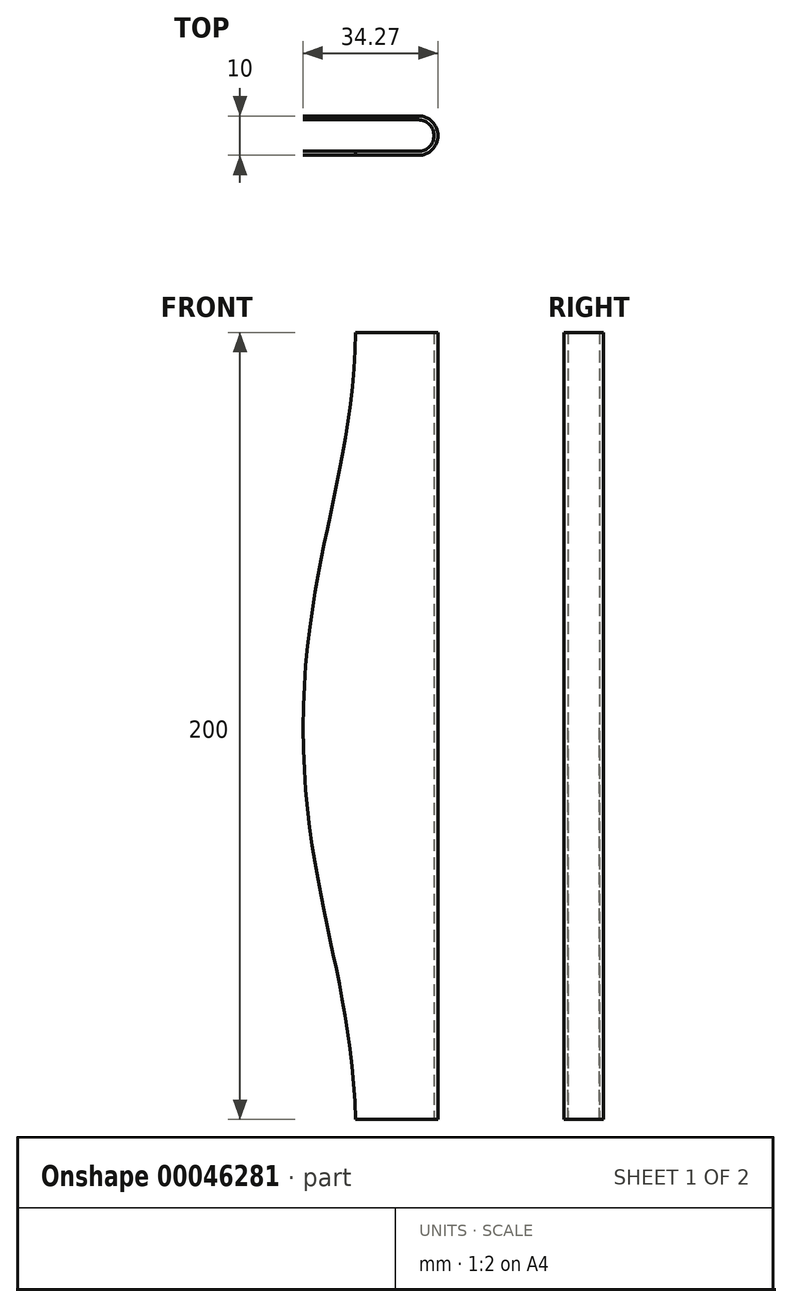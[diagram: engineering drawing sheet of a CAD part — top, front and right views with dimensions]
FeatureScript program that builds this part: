
annotation { "Feature Type Name" : "Feature", "Feature Type Description" : "" }
export const myFeature = defineFeature(function(context is Context, id is Id, definition is map)
    precondition{}
    {
        {
            var Q0;
            Q0=qCreatedBy(makeId("Top.planeOp"),FACE);
            var sketch = newSketch(context, id + "F0", { "sketchPlane" : qUnion([Q0])});
            skArc(sketch, "E0", {"start": v(0, -4) * mm, "mid": v(4, 0) * mm, "end": v(0, 4) * mm});
            skLineSegment(sketch, "E1", {"start": v(0, 0) * mm, "end": v(0, 4) * mm, "construction": true});
            skLineSegment(sketch, "E2", {"start": v(0, 4) * mm, "end": v(-30.1, 4) * mm});
            skLineSegment(sketch, "E3", {"start": v(0, 0) * mm, "end": v(-14, 0) * mm, "construction": true});
            skLineSegment(sketch, "E4", {"start": v(0, 0) * mm, "end": v(0, -4) * mm, "construction": true});
            skLineSegment(sketch, "E5.MirrorCS", {"start": v(0, -4) * mm, "end": v(-30.1, -4) * mm});
            skLineSegment(sketch, "E6.0", {"start": v(0, 5) * mm, "end": v(-30.1, 5) * mm});
            skArc(sketch, "E6.1", {"start": v(0, -5) * mm, "mid": v(5, 0) * mm, "end": v(0, 5) * mm});
            skLineSegment(sketch, "E6.2", {"start": v(0, -5) * mm, "end": v(-30.1, -5) * mm});
            skLineSegment(sketch, "E7", {"start": v(-30.1, 4) * mm, "end": v(-30.1, 5) * mm});
            skLineSegment(sketch, "E8", {"start": v(-30.1, -4) * mm, "end": v(-30.1, -5) * mm});
            skSolve(sketch);
        }
        {
            var Q0;
            Q0=makeQuery(id+"F0.imprint","IMPRINT",FACE,{"disambiguationData":[TD([[makeQuery(id+"F0.imprint","IMPRINT",EDGE,{"derivedFrom":sQuery(id+"F0.wireOp",EDGE,"E0")}),-1.0]])]});
            extrude(context, id + "F1", {"entities" : qUnion([Q0]), "depth" : 200 * mm});
        }
        {
            var Q0;
            Q0=qCreatedBy(makeId("Front.planeOp"),FACE);
            var sketch = newSketch(context, id + "F2", { "sketchPlane" : qUnion([Q0])});
            skLineSegment(sketch, "E9", {"start": v(0, 200.25) * mm, "end": v(-15.93, 200.25) * mm, "construction": true});
            skLineSegment(sketch, "E10", {"start": v(-15.93, 200.25) * mm, "end": v(-15.93, 211.97) * mm});
            skLineSegment(sketch, "E11", {"start": v(0, 200.25) * mm, "end": v(0, 99.54) * mm});
            skLineSegment(sketch, "E12", {"start": v(0, 99.54) * mm, "end": v(-39.41, 99.54) * mm, "construction": true});
            skLineSegment(sketch, "E13", {"start": v(-29.27, 99.54) * mm, "end": v(-29.27, 84.1) * mm, "construction": true});
            skFitSpline(sketch, "E14", {"points": [v(-15.93, 200.25) * mm, v(-19.73, 166.47) * mm, v(-25.1, 140.16) * mm, v(-29.27, 99.54) * mm], "startDerivative": vector(-1.09, -107.09) * mm, "endDerivative": vector(-0.1, -128.78) * mm});
            skFitSpline(sketch, "E15.MirrorCS", {"points": [v(-15.93, -1.17) * mm, v(-19.73, 32.61) * mm, v(-25.1, 58.91) * mm, v(-29.27, 99.54) * mm], "startDerivative": vector(-1.09, 107.09) * mm, "endDerivative": vector(-0.1, 128.78) * mm});
            skLineSegment(sketch, "E16.MirrorCS", {"start": v(-15.93, -1.17) * mm, "end": v(-15.93, -12.9) * mm});
            skLineSegment(sketch, "E17", {"start": v(-15.93, 211.97) * mm, "end": v(-58.8, 211.97) * mm});
            skLineSegment(sketch, "E18", {"start": v(-58.8, 211.97) * mm, "end": v(-58.8, -9.85) * mm});
            skLineSegment(sketch, "E19", {"start": v(-15.93, -12.9) * mm, "end": v(-58.8, -9.85) * mm});
            skSolve(sketch);
        }
        {
            var Q0;
            Q0=makeQuery(id+"F2.imprint","IMPRINT",FACE,{"disambiguationData":[TD([[makeQuery(id+"F2.imprint","IMPRINT",EDGE,{"derivedFrom":sQuery(id+"F2.wireOp",EDGE,"E10")}),1.0]])]});
            extrude(context, id + "F3", {"entities" : qUnion([Q0]), "operationType" : NewBodyOperationType.REMOVE, "endBound" : BoundingType.SYMMETRIC, "depth" : 25 * mm});
        }
    });
